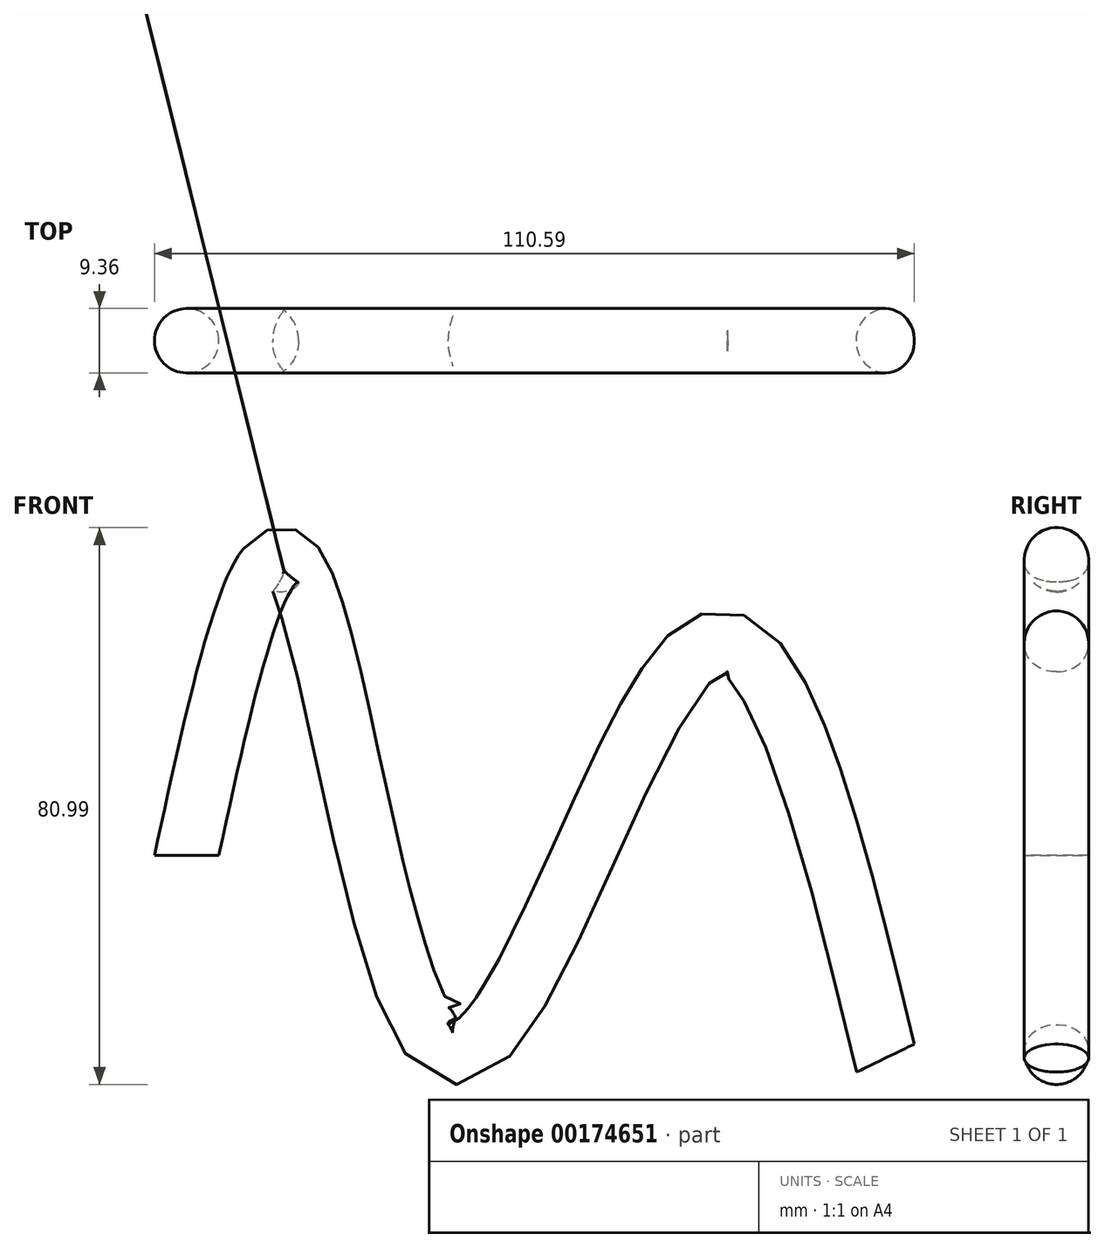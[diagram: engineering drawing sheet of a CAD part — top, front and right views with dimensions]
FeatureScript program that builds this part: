
annotation { "Feature Type Name" : "Feature", "Feature Type Description" : "" }
export const myFeature = defineFeature(function(context is Context, id is Id, definition is map)
    precondition{}
    {
        {
            var Q0;
            Q0=qCreatedBy(makeId("Front.planeOp"),FACE);
            var sketch = newSketch(context, id + "F0", { "sketchPlane" : qUnion([Q0])});
            skFitSpline(sketch, "E0", {"points": [v(-61.9, 0) * mm, v(-46.32, 41.92) * mm, v(-23.09, -28.61) * mm, v(12.6, 29.74) * mm, v(39.8, -29.46) * mm], "startDerivative": vector(74.78, 345.07) * mm, "endDerivative": vector(95.35, -395.3) * mm});
            skSolve(sketch);
        }
        {
            var Q0;
            Q0=qCreatedBy(makeId("Top.planeOp"),FACE);
            var Q1;
            Q1=sQuery(id+"F0.wireOp",VERTEX,"E0.start");
            cPlane(context, id + "F1", {"entities" : qUnion([Q0, Q1]), "cplaneType" : CPlaneType.PLANE_POINT, "offset" : 25 * mm, "width" : 150 * mm, "height" : 150 * mm});
        }
        {
            var Q0;
            Q0=qCreatedBy(id+"F1.planeOp",FACE);
            var sketch = newSketch(context, id + "F2", { "sketchPlane" : qUnion([Q0])});
            skCircle(sketch, "E1", {"center": v(-61.9, 0) * mm, "radius": 4.68 * mm});
            skSolve(sketch);
        }
        {
            var Q0;
            Q0=makeQuery(id+"F2.imprint","IMPRINT",FACE,{"disambiguationData":[TD([[makeQuery(id+"F2.imprint","IMPRINT",EDGE,{"derivedFrom":sQuery(id+"F2.wireOp",EDGE,"E1")}),1.0]])]});
            var Q1;
            Q1=sQuery(id+"F0.wireOp",EDGE,"E0");
            sweep(context, id + "F3", {"profiles" : qUnion([Q0]), "path" : qUnion([Q1])});
        }
    });
